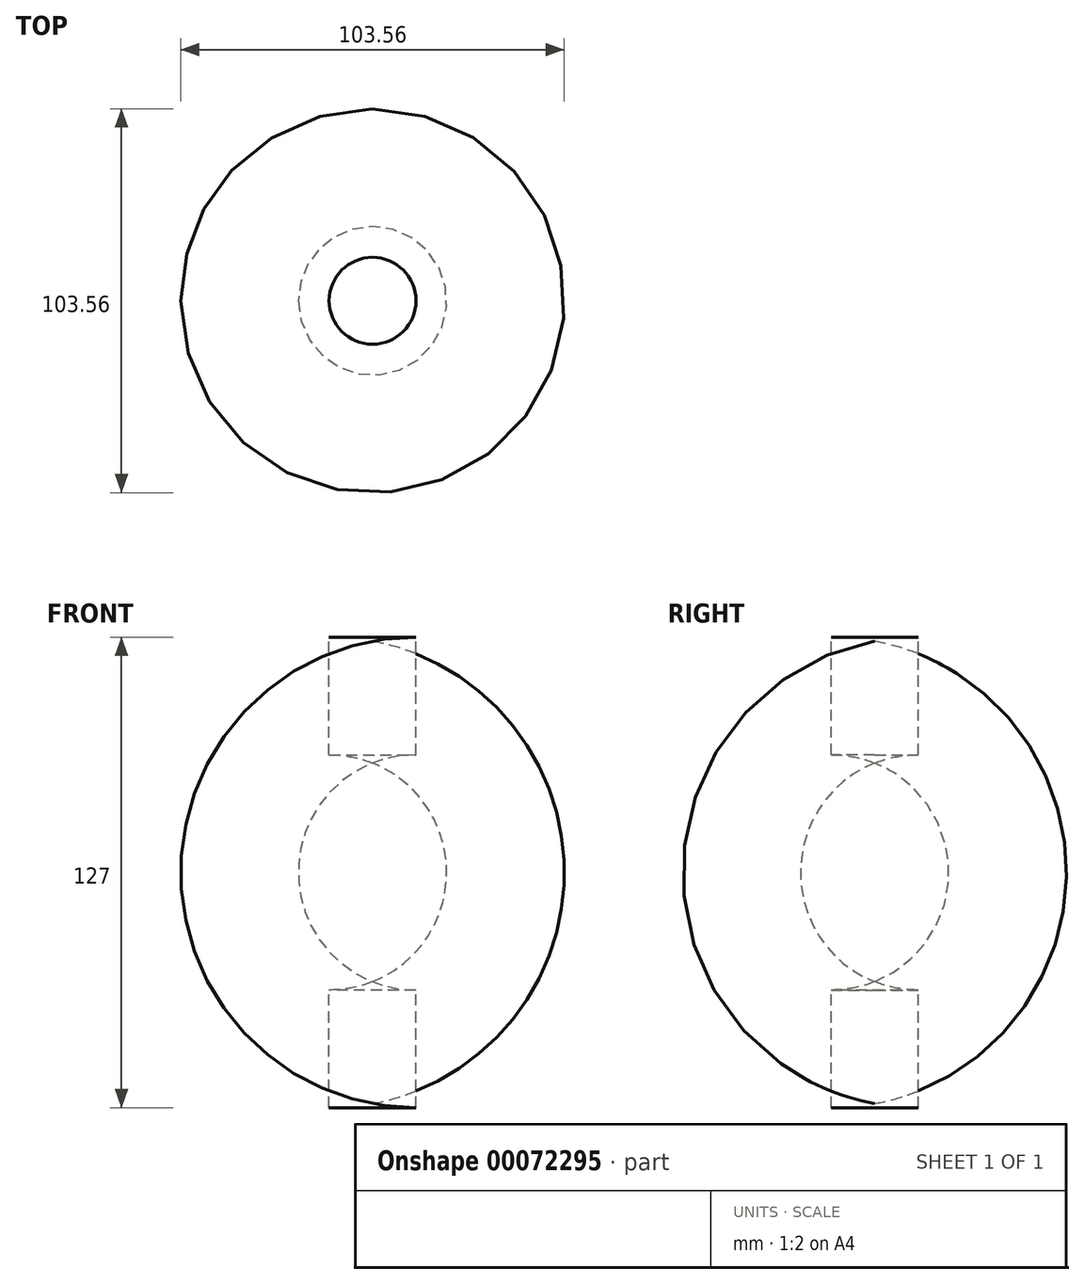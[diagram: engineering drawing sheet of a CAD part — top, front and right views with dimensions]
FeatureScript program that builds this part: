
annotation { "Feature Type Name" : "Feature", "Feature Type Description" : "" }
export const myFeature = defineFeature(function(context is Context, id is Id, definition is map)
    precondition{}
    {
        {
            var Q0;
            Q0=qCreatedBy(makeId("Top.planeOp"),FACE);
            var sketch = newSketch(context, id + "F0", { "sketchPlane" : qUnion([Q0])});
            skCircle(sketch, "E0", {"center": v(0, 0) * mm, "radius": 75.22 * mm});
            skSolve(sketch);
        }
        {
            var Q0;
            Q0=makeQuery(id+"F0.imprint","IMPRINT",FACE,{"disambiguationData":[TD([[makeQuery(id+"F0.imprint","IMPRINT",EDGE,{"derivedFrom":sQuery(id+"F0.wireOp",EDGE,"E0")}),1.0]])]});
            extrude(context, id + "F1", {"entities" : qUnion([Q0]), "depth" : 63.5 * mm});
        }
        {
            var Q0;
            Q0=makeQuery(id+"F1.opExtrude","CAP_FACE",FACE,{"disambiguationData":[OSD([sQuery(id+"F0.wireOp",EDGE,"E0")])],"isStart":true});
            extrude(context, id + "F2", {"entities" : qUnion([Q0]), "operationType" : NewBodyOperationType.ADD, "depth" : 63.5 * mm});
        }
        {
            var Q0;
            Q0=makeQuery(id+"F2.opExtrude","CAP_EDGE",EDGE,{"disambiguationData":[OSD([sQuery(id+"F0.wireOp",EDGE,"E0")])],"isStart":false});
            var Q1;
            {var subQ0=sQuery(id+"F0.wireOp",EDGE,"E0");Q1=makeQuery(id+"F2.boolean.opBoolean","MERGE",FACE,{"derivedFrom":[makeQuery(id+"F1.opExtrude","SWEPT_FACE",FACE,{"disambiguationData":[OSD([subQ0])]}),makeQuery(id+"F2.opExtrude","SWEPT_FACE",FACE,{"disambiguationData":[OSD([subQ0])]})]});}
            fillet(context, id + "F3", {"entities" : qUnion([Q0, Q1]), "radius" : 63.5 * mm, "tangentPropagation" : true, "allowEdgeOverflow" : false});
        }
        {
            var Q0;
            Q0=makeQuery(id+"F1.opExtrude","CAP_FACE",FACE,{"disambiguationData":[OSD([sQuery(id+"F0.wireOp",EDGE,"E0")])],"isStart":false});
            var Q1;
            Q1=makeQuery(id+"F2.opExtrude","CAP_FACE",FACE,{"disambiguationData":[OSD([sQuery(id+"F0.wireOp",EDGE,"E0")])],"isStart":false});
            shell(context, id + "F4", {"entities" : qUnion([Q0, Q1]), "thickness" : 31.75 * mm});
        }
    });
